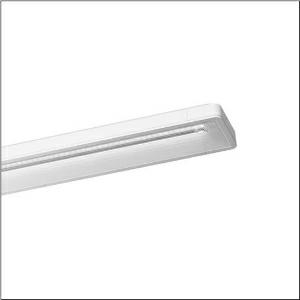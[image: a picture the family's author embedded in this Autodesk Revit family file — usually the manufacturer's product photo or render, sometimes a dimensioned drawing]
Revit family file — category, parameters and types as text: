
# Revit family: taris_r__21_5mt216704wd_b9ab
name_source: partatom
category: Lighting Fixtures
units: mm (PartAtom-declared; Revit-internal decimal feet)

## family parameters
Cut with Voids When Loaded = No
Host = Face
Light Source = No
Part Type = Normal
Room Calculation Point = No
Round Connector Dimension = Use Diameter
Shared = No

## types (1)
- Taris® 21 (1 x LED, 4910 lm, 30.6 W, 4000K)
    Apparent Load = 31 VA
    CIE Flux Codes = 73 96 99 100 100
    Color Rendering = 80
    Color Temperature = 4000K
    Default Elevation = 1800 mm
    Description = Taris® 21, office luminaire, primary anti-glare with micro louvre, primary optical cover: axial lens, of PMMA, structured, CAT 2 (L<= 1500cd/m²), light emission: direct distribution, primary light characteristic: symmetric, installation type: surface-mounted, LED rated luminous flux: 4.910 lm, light colour: 840, colour temperature: 4000K, control gear: ECG, with terminal, 5-pole, mains connection: 230V, AC, 50Hz, rated input power: 31W, housing, luminaire housing, of plastic, traffic white (RAL 9016), length: 1.230 mm, width: 134 mm, height: 50mm, protection rating (complete): IP20, insulation class (complete): insulation class I (protective earthing), certification: CE, ENEC, VDE, protection symbol: F, impact resistance: IK02, permissible ambient temperature for indoor applications: 0..+35°C, standard: EN 50419, packaging unit: 1 piece
    Height = 51 mm
    Lamp = 1 x LED
    Lamp Light Flux = 4910 lm
    Lamp Power = 30.6 W
    Lamp count = 1
    Length = 1233 mm
    Luminous efficacy = 160 lm/W
    Manufacturer = Siteco
    ModVariant = No
    Model = 5MT216704WD
    Mounting Place = Ceiling
    Mounting Type = Surface mounted
    Number of Poles = 1
    OnlyDefault = Yes
    Power Factor = 1
    Product Name = Taris® 21
    Product group = office luminaire | ceiling mounted
    ProductGroupID = 302
    Protection Class = Protection class I
    Protection Degree = IP 20
    RLX_Detail_Level = 1
    RlxData = <blob elided: 38937 chars, md5=636b9d60>
    Socket = socket
    Standby Power = 0 W
    System Light Flux = 4910 lm
    System Power = 31 W
    Type Comments = Product without accessories
    Type Image = l_1004728.jpg
    URL = http://relux.com
    VarID = ---
    Voltage = 0 V
    Weight = 0.00 kg
    Width = 134 mm

## geometry (parser evidence)
native form markers: Blend x4, Sweep x10
no freeform markers — native parametric forms only
